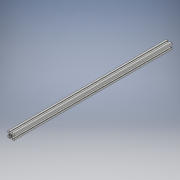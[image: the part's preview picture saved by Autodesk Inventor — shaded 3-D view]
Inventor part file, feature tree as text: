
AUTODESK INVENTOR PART (.ipt)
format: ipt  version: 2019 (Build 230136000, 136)  size: 239,616 bytes
history: native  units: mm
features: extrude x1, sketch x1
ambient origin geometry x8: Origin, YZ Plane, XZ Plane, XY Plane, X Axis, Y Axis, Z Axis, Center Point
bodies: Solid1 (feature_tree)
feature tree (2):
  extrude  "Extrusion1"  [1 undecoded]
  sketch  "Sketch_1"  dims[d0=500.0mm d1=0.0mm]
note: 1 required parameter value undecoded (feature->parameter linkage not recoverable at this tier; creation-order binding heuristic only, values carry confidence <= 0.55)
